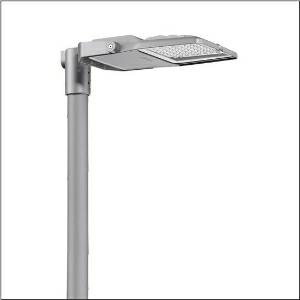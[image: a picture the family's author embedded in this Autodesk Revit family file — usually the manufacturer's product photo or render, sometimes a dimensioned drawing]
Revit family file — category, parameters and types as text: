
# Revit family: floodlight_fl_21_iq_mini___pl43_5xa7771c4a3a_be4f
name_source: partatom
category: Lighting Fixtures
units: mm (PartAtom-declared; Revit-internal decimal feet)

## family parameters
Cut with Voids When Loaded = No
Host = Face
Light Source = No
Part Type = Normal
Room Calculation Point = No
Round Connector Dimension = Use Diameter
Shared = No

## types (1)
- --- (1 x LED, 13050 lm, 87.2 W, 4000K)
    Apparent Load = 87 VA
    CIE Flux Codes = 27 78 99 100 100
    Color Rendering = 70
    Color Temperature = 4000K
    Default Elevation = 1800 mm
    Description = Floodlight FL 21 iQ mini, floodlight, primary light control with lens, of PMMA, primary optical cover: protective disc, of toughened safety glass, transparent, light distribution: PL43, light emission: direct distribution, installation type: surface-mounted, lamps: LED, High Power LED, rated values: 13.050lm | 87,2W | 149,7lm/W (begin service life); end service life: 13.050lm | 92,1W; at 50% lumin. flux: 6.525lm | 40,2W | 162,3lm/W, colour temperature: 4000K, colour rendering: CRI > 70, light colour: 740, light setting 1 begin service life: 100% | 13.050lm | 87,2W | 149,7lm/W | 4.000K, light setting 1 end service life: 92,1W, further light settings possible, control: Auto-Match, Temp-Guard, Lumen-Switch, Night-Set, Smart-Wire, Light-Fading, Desk-Remote (wireless, voltage-free reading and setting of iQ features in the workshop via application-optimized NFC function/RFID function), optimised constant luminous flux control (CLO 2.0), pre-setting: linear dimming characteristic, with terminal, 6-pole, mains connection: 220..240V, AC, 50/60Hz, luminaire housing, of diecast aluminium, powder-coated, SITECO metallic grey (DB 702S), corrosivity category C5 mid according to DIN EN ISO 12944suitable for swimming poolschlorine-resistant, sealing non-destructively replaceable, please order mast flange separately, mast bracket, of steel, galvanised, powder-coated, SITECO metallic grey (DB 702S), protection rating (complete): IP66, insulation class (complete): insulation class II (safety insulation), certification: CE, ENEC, VDE, protection symbol: D, impact resistance: IK08, permissible operating ambient temperature: -40..+40°C, permissible operating ambient temperature for outdoor applications: -40..+50°C, standard: DIN EN 12944, LABS conformity tested according to VDMA 24364:2018-05, packaging unit: 1 piece

Light Distribution: PL43
    Height = 70 mm
    Lamp = 1 x LED
    Lamp Light Flux = 13050 lm
    Lamp Power = 87.2 W
    Lamp count = 1
    Length = 485 mm
    Luminous efficacy = 150 lm/W
    Manufacturer = Siteco
    ModVariant = No
    Model = 5XA7771C4A3A
    Number of Poles = 1
    OnlyDefault = Yes
    Power Factor = 1
    Product Name = Floodlight FL 21 iQ mini | PL43
    Product group = floodlight | pylon annexe
    ProductGroupID = 6201
    Protection Class = Protection class II
    Protection Degree = IP 66
    RLX_Detail_Level = 1
    RLX_Emergency_Light_Flux = 0 lm
    RLX_Emergency_Type = 0
    RLX_Emergency_Type_DB = No
    RlxData = <blob elided: 101441 chars, md5=2c7d9b98>
    Socket = socket
    Standby Power = 0 W
    System Light Flux = 13050 lm
    System Power = 87 W
    Type Comments = factory setting: luminous flux: 100 % | dim-lin: 254 | 456 mA
    Type Image = l_1007125.jpg
    URL = http://relux.com
    VarID = @adj_161891
    Voltage = 0 V
    Weight = 0.00 kg
    Width = 337 mm

## geometry (parser evidence)
native form markers: Blend x4, Sweep x13
no freeform markers — native parametric forms only
